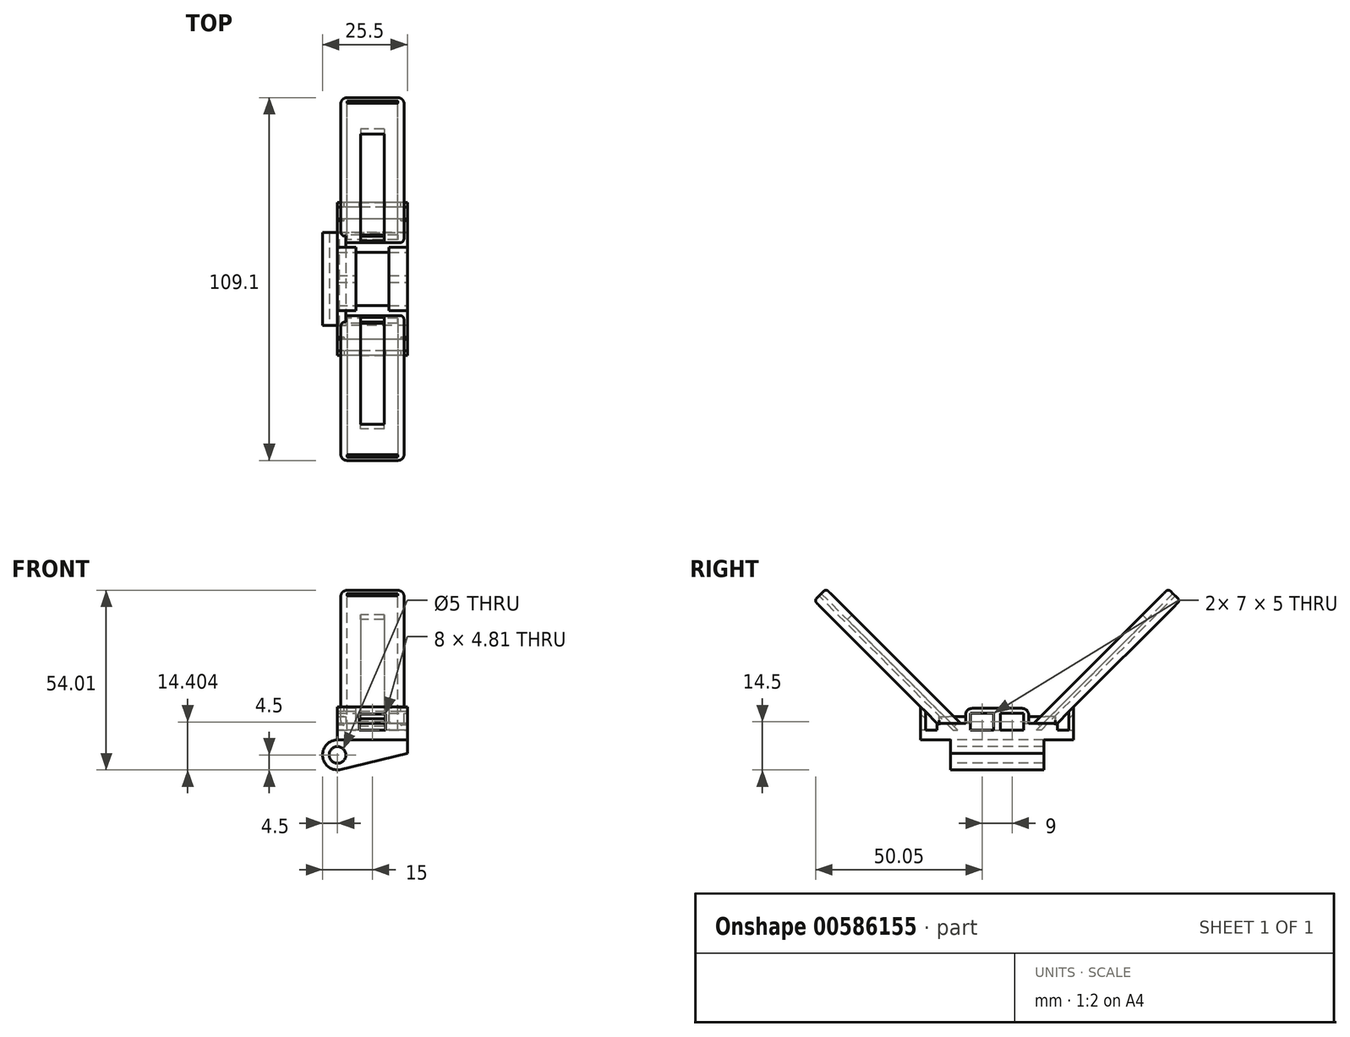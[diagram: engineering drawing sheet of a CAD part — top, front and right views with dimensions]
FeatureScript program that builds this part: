
annotation { "Feature Type Name" : "Feature", "Feature Type Description" : "" }
export const myFeature = defineFeature(function(context is Context, id is Id, definition is map)
    precondition{}
    {
        {
            var Q0;
            Q0=qCreatedBy(makeId("Top.planeOp"),FACE);
            var sketch = newSketch(context, id + "F0", { "sketchPlane" : qUnion([Q0])});
            skLineSegment(sketch, "E0.bottom", {"start": v(-10.5, 23) * mm, "end": v(10.5, 23) * mm});
            skLineSegment(sketch, "E0.top", {"start": v(-10.5, -23) * mm, "end": v(10.5, -23) * mm});
            skLineSegment(sketch, "E0.left", {"start": v(-10.5, 23) * mm, "end": v(-10.5, -23) * mm});
            skLineSegment(sketch, "E0.right", {"start": v(10.5, 23) * mm, "end": v(10.5, -23) * mm});
            skPoint(sketch, "E0.middle", {"position": v(0, 0) * mm});
            skSolve(sketch);
        }
        {
            var Q0;
            Q0=qSketchRegion(id+"F0",true);
            extrude(context, id + "F1", {"entities" : qUnion([Q0]), "oppositeDirection" : true, "depth" : 12 * mm, "offsetDistance" : 25 * mm});
        }
        {
            var Q0;
            Q0=qCreatedBy(makeId("Front.planeOp"),FACE);
            var sketch = newSketch(context, id + "F2", { "sketchPlane" : qUnion([Q0])});
            skCircle(sketch, "E1", {"center": v(-10.5, -7.5) * mm, "radius": 4.5 * mm});
            skPoint(sketch, "E1.first.point", {"position": v(-10.5, -3) * mm});
            skPoint(sketch, "E1.second.point", {"position": v(-10.5, -12) * mm});
            skPoint(sketch, "E1.third.point", {"position": v(-14.85, -8.64) * mm});
            skPoint(sketch, "E2.first.point", {"position": v(10.5, 0) * mm});
            skPoint(sketch, "E2.second.point", {"position": v(10.5, -12) * mm});
            skPoint(sketch, "E2.third.point", {"position": v(4.96, -4.94) * mm});
            skSolve(sketch);
        }
        {
            var Q0;
            Q0=makeQuery(id+"F2.imprint","IMPRINT",FACE,{"disambiguationData":[TD([[makeQuery(id+"F2.imprint","IMPRINT",EDGE,{"derivedFrom":sQuery(id+"F2.wireOp",EDGE,"E1")}),1.0]])]});
            extrude(context, id + "F3", {"entities" : qUnion([Q0]), "operationType" : NewBodyOperationType.ADD, "endBound" : BoundingType.SYMMETRIC, "oppositeDirection" : true, "depth" : 46 * mm, "offsetDistance" : 25 * mm});
        }
        {
            var Q0;
            Q0=qCreatedBy(makeId("Top.planeOp"),FACE);
            var sketch = newSketch(context, id + "F4", { "sketchPlane" : qUnion([Q0])});
            skLineSegment(sketch, "E3", {"start": v(-22.5, -9) * mm, "end": v(32.95, -9) * mm});
            skSolve(sketch);
        }
        {
            var Q0;
            Q0=sQuery(id+"F4.wireOp",EDGE,"E3");
            cPlane(context, id + "F5", {"entities" : qUnion([Q0]), "cplaneType" : CPlaneType.LINE_ANGLE, "offset" : 25 * mm, "angle" : 45 * degree, "width" : 150 * mm, "height" : 150 * mm});
        }
        {
            var Q0;
            Q0=qCreatedBy(id+"F5.planeOp",FACE);
            var sketch = newSketch(context, id + "F6", { "sketchPlane" : qUnion([Q0])});
            skLineSegment(sketch, "E4.bottom", {"start": v(9.5, 6.36) * mm, "end": v(-9.5, 6.36) * mm});
            skLineSegment(sketch, "E4.top", {"start": v(9.5, 66.36) * mm, "end": v(-9.5, 66.36) * mm});
            skLineSegment(sketch, "E4.left", {"start": v(9.5, 6.36) * mm, "end": v(9.5, 66.36) * mm});
            skLineSegment(sketch, "E4.right", {"start": v(-9.5, 6.36) * mm, "end": v(-9.5, 66.36) * mm});
            skSolve(sketch);
        }
        {
            var Q0;
            Q0=qSketchRegion(id+"F6",true);
            extrude(context, id + "F7", {"entities" : qUnion([Q0]), "operationType" : NewBodyOperationType.ADD, "oppositeDirection" : true, "depth" : 5 * mm, "offsetDistance" : 25 * mm});
        }
        {
            var Q0;
            Q0=makeQuery(id+"F7.opExtrude","SWEPT_EDGE",EDGE,{"disambiguationData":[OSD([sQuery(id+"F6.wireOp",EDGE,"E4.top"),sQuery(id+"F6.wireOp",EDGE,"E4.left")])]});
            var Q1;
            Q1=makeQuery(id+"F7.opExtrude","SWEPT_EDGE",EDGE,{"disambiguationData":[OSD([sQuery(id+"F6.wireOp",EDGE,"E4.top"),sQuery(id+"F6.wireOp",EDGE,"E4.right")])]});
            fillet(context, id + "F8", {"entities" : qUnion([Q0, Q1]), "radius" : (2) * mm, "tangentPropagation" : true, "allowEdgeOverflow" : false});
        }
        {
            var Q0;
            Q0=makeQuery(id+"F7.opExtrude","CAP_EDGE",EDGE,{"disambiguationData":[OSD([sQuery(id+"F6.wireOp",EDGE,"E4.right")])],"isStart":true});
            var Q1;
            Q1=makeQuery(id+"F7.opExtrude","CAP_EDGE",EDGE,{"disambiguationData":[OSD([sQuery(id+"F6.wireOp",EDGE,"E4.right")])],"isStart":false});
            var Q2;
            Q2=makeQuery(id+"F7.opExtrude","CAP_EDGE",EDGE,{"disambiguationData":[OSD([sQuery(id+"F6.wireOp",EDGE,"E4.left")])],"isStart":true});
            var Q3;
            Q3=makeQuery(id+"F7.opExtrude","CAP_EDGE",EDGE,{"disambiguationData":[OSD([sQuery(id+"F6.wireOp",EDGE,"E4.left")])],"isStart":false});
            fillet(context, id + "F9", {"entities" : qUnion([Q0, Q1, Q2, Q3]), "radius" : 1 * mm, "tangentPropagation" : true, "allowEdgeOverflow" : false});
        }
        {
            var Q0;
            Q0=qCreatedBy(makeId("Right.planeOp"),FACE);
            var sketch = newSketch(context, id + "F10", { "sketchPlane" : qUnion([Q0])});
            skLineSegment(sketch, "E5.bottom", {"start": v(-9.5, 6.5) * mm, "end": v(9.5, 6.5) * mm});
            skLineSegment(sketch, "E5.top", {"start": v(-9.5, 0) * mm, "end": v(9.5, 0) * mm});
            skLineSegment(sketch, "E5.left", {"start": v(-9.5, 6.5) * mm, "end": v(-9.5, 0) * mm});
            skLineSegment(sketch, "E5.right", {"start": v(9.5, 6.5) * mm, "end": v(9.5, 0) * mm});
            skSolve(sketch);
        }
        {
            var Q0;
            Q0=qSketchRegion(id+"F10",true);
            extrude(context, id + "F11", {"entities" : qUnion([Q0]), "operationType" : NewBodyOperationType.ADD, "endBound" : BoundingType.SYMMETRIC, "depth" : 21 * mm, "offsetDistance" : 25 * mm});
        }
        {
            var Q0;
            Q0=makeQuery(id+"F11.opExtrude","SWEPT_EDGE",EDGE,{"disambiguationData":[OSD([sQuery(id+"F10.wireOp",EDGE,"E5.bottom"),sQuery(id+"F10.wireOp",EDGE,"E5.left")])]});
            var Q1;
            Q1=makeQuery(id+"F11.opExtrude","SWEPT_EDGE",EDGE,{"disambiguationData":[OSD([sQuery(id+"F10.wireOp",EDGE,"E5.bottom"),sQuery(id+"F10.wireOp",EDGE,"E5.right")])]});
            fillet(context, id + "F12", {"entities" : qUnion([Q0, Q1]), "radius" : 2 * mm, "tangentPropagation" : true, "allowEdgeOverflow" : false});
        }
        {
            var Q0;
            Q0=qCreatedBy(makeId("Right.planeOp"),FACE);
            var sketch = newSketch(context, id + "F13", { "sketchPlane" : qUnion([Q0])});
            skLineSegment(sketch, "E6.bottom", {"start": v(-8, 0) * mm, "end": v(-1, 0) * mm});
            skLineSegment(sketch, "E6.top", {"start": v(-8, 5) * mm, "end": v(-1, 5) * mm});
            skLineSegment(sketch, "E6.left", {"start": v(-8, 0) * mm, "end": v(-8, 5) * mm});
            skLineSegment(sketch, "E6.right", {"start": v(-1, 0) * mm, "end": v(-1, 5) * mm});
            skLineSegment(sketch, "E7.bottom", {"start": v(8, 0) * mm, "end": v(1, 0) * mm});
            skLineSegment(sketch, "E7.top", {"start": v(8, 5) * mm, "end": v(1, 5) * mm});
            skLineSegment(sketch, "E7.left", {"start": v(8, 0) * mm, "end": v(8, 5) * mm});
            skLineSegment(sketch, "E7.right", {"start": v(1, 0) * mm, "end": v(1, 5) * mm});
            skSolve(sketch);
        }
        {
            var Q0;
            Q0=qSketchRegion(id+"F13",true);
            extrude(context, id + "F14", {"entities" : qUnion([Q0]), "operationType" : NewBodyOperationType.REMOVE, "endBound" : BoundingType.SYMMETRIC, "oppositeDirection" : true, "depth" : 55 * mm, "offsetDistance" : 25 * mm});
        }
        {
            var Q0;
            Q0=qCreatedBy(makeId("Right.planeOp"),FACE);
            var sketch = newSketch(context, id + "F15", { "sketchPlane" : qUnion([Q0])});
            skLineSegment(sketch, "E8.bottom", {"start": v(-9.5, 0) * mm, "end": v(9.5, 0) * mm});
            skLineSegment(sketch, "E8.top", {"start": v(-9.5, 6.5) * mm, "end": v(9.5, 6.5) * mm});
            skLineSegment(sketch, "E8.left", {"start": v(-9.5, 0) * mm, "end": v(-9.5, 6.5) * mm});
            skLineSegment(sketch, "E8.right", {"start": v(9.5, 0) * mm, "end": v(9.5, 6.5) * mm});
            skSolve(sketch);
        }
        {
            var Q0;
            Q0=qSketchRegion(id+"F15",true);
            extrude(context, id + "F16", {"entities" : qUnion([Q0]), "operationType" : NewBodyOperationType.REMOVE, "endBound" : BoundingType.SYMMETRIC, "oppositeDirection" : true, "depth" : 10 * mm, "offsetDistance" : 25 * mm});
        }
        {
            var Q0;
            Q0=makeQuery(id+"F7.opExtrude","SWEPT_FACE",FACE,{"disambiguationData":[OSD([sQuery(id+"F6.wireOp",EDGE,"E4.top")])]});
            var sketch = newSketch(context, id + "F17", { "sketchPlane" : qUnion([Q0])});
            skLineSegment(sketch, "E9.bottom", {"start": v(-7.6, -8.36) * mm, "end": v(7.6, -8.36) * mm});
            skLineSegment(sketch, "E9.top", {"start": v(-7.6, -9.36) * mm, "end": v(7.6, -9.36) * mm});
            skLineSegment(sketch, "E9.left", {"start": v(-7.6, -8.36) * mm, "end": v(-7.6, -9.36) * mm});
            skLineSegment(sketch, "E9.right", {"start": v(7.6, -8.36) * mm, "end": v(7.6, -9.36) * mm});
            skSolve(sketch);
        }
        {
            var Q0;
            Q0=qSketchRegion(id+"F17",true);
            extrude(context, id + "F18", {"entities" : qUnion([Q0]), "operationType" : NewBodyOperationType.REMOVE, "oppositeDirection" : true, "depth" : 58.5 * mm, "offsetDistance" : 25 * mm});
        }
        {
            var Q0;
            Q0=makeQuery(id+"F7.opExtrude","CAP_FACE",FACE,{"disambiguationData":[OSD([sQuery(id+"F6.wireOp",EDGE,"E4.bottom"),sQuery(id+"F6.wireOp",EDGE,"E4.top"),sQuery(id+"F6.wireOp",EDGE,"E4.left"),sQuery(id+"F6.wireOp",EDGE,"E4.right")])],"isStart":true});
            var sketch = newSketch(context, id + "F19", { "sketchPlane" : qUnion([Q0])});
            skLineSegment(sketch, "E10.bottom", {"start": v(-3.5, 55.36) * mm, "end": v(3.5, 55.36) * mm});
            skLineSegment(sketch, "E10.top", {"start": v(-3.5, 9.86) * mm, "end": v(3.5, 9.86) * mm});
            skLineSegment(sketch, "E10.left", {"start": v(-3.5, 55.36) * mm, "end": v(-3.5, 9.86) * mm});
            skLineSegment(sketch, "E10.right", {"start": v(3.5, 55.36) * mm, "end": v(3.5, 9.86) * mm});
            skSolve(sketch);
        }
        {
            var Q0;
            Q0=qSketchRegion(id+"F19",true);
            extrude(context, id + "F20", {"entities" : qUnion([Q0]), "operationType" : NewBodyOperationType.REMOVE, "oppositeDirection" : true, "depth" : 2 * mm, "offsetDistance" : 25 * mm});
        }
        {
            var Q0;
            Q0=qCreatedBy(makeId("Front.planeOp"),FACE);
            var sketch = newSketch(context, id + "F21", { "sketchPlane" : qUnion([Q0])});
            skCircle(sketch, "E11", {"center": v(-10.5, -7.5) * mm, "radius": 2.5 * mm});
            skSolve(sketch);
        }
        {
            var Q0;
            Q0 = qSketchRegion(id + "F21", true);
            extrude(context, id + "F22", {"entities" : qUnion([Q0]), "operationType" : NewBodyOperationType.REMOVE, "endBound" : BoundingType.SYMMETRIC, "oppositeDirection" : true, "depth" : 46 * mm, "offsetDistance" : 25 * mm});
        }
        {
            var Q0;
            Q0=makeQuery(id+"F3.boolean.opBoolean","MERGE",FACE,{"derivedFrom":[makeQuery(id+"F1.opExtrude","SWEPT_FACE",FACE,{"disambiguationData":[OSD([sQuery(id+"F0.wireOp",EDGE,"E0.top")])]}),makeQuery(id+"F3.opExtrude","CAP_FACE",FACE,{"disambiguationData":[OSD([sQuery(id+"F2.wireOp",EDGE,"E1")])],"isStart":true})]});
            var sketch = newSketch(context, id + "F23", { "sketchPlane" : qUnion([Q0])});
            skLineSegment(sketch, "E12.bottom", {"start": v(20, -12) * mm, "end": v(-20, -12) * mm});
            skLineSegment(sketch, "E12.top", {"start": v(20, -3) * mm, "end": v(-20, -3) * mm});
            skLineSegment(sketch, "E12.left", {"start": v(20, -12) * mm, "end": v(20, -3) * mm});
            skLineSegment(sketch, "E12.right", {"start": v(-20, -12) * mm, "end": v(-20, -3) * mm});
            skSolve(sketch);
        }
        {
            var Q0;
            Q0 = qSketchRegion(id + "F23", true);
            extrude(context, id + "F24", {"entities" : qUnion([Q0]), "operationType" : NewBodyOperationType.REMOVE, "oppositeDirection" : true, "depth" : 9 * mm, "offsetDistance" : 25 * mm});
        }
        {
            var Q0;
            Q0=makeQuery(id+"F3.boolean.opBoolean","MERGE",FACE,{"derivedFrom":[makeQuery(id+"F1.opExtrude","SWEPT_FACE",FACE,{"disambiguationData":[OSD([sQuery(id+"F0.wireOp",EDGE,"E0.bottom")])]}),makeQuery(id+"F3.opExtrude","CAP_FACE",FACE,{"disambiguationData":[OSD([sQuery(id+"F2.wireOp",EDGE,"E1")])],"isStart":false})]});
            var sketch = newSketch(context, id + "F25", { "sketchPlane" : qUnion([Q0])});
            skLineSegment(sketch, "E13.bottom", {"start": v(-20, -3) * mm, "end": v(20, -3) * mm});
            skLineSegment(sketch, "E13.top", {"start": v(-20, -12) * mm, "end": v(20, -12) * mm});
            skLineSegment(sketch, "E13.left", {"start": v(-20, -3) * mm, "end": v(-20, -12) * mm});
            skLineSegment(sketch, "E13.right", {"start": v(20, -3) * mm, "end": v(20, -12) * mm});
            skSolve(sketch);
        }
        {
            var Q0;
            Q0 = qSketchRegion(id + "F25", true);
            extrude(context, id + "F26", {"entities" : qUnion([Q0]), "operationType" : NewBodyOperationType.REMOVE, "oppositeDirection" : true, "depth" : 9 * mm, "offsetDistance" : 25 * mm});
        }
        {
            var Q0;
            Q0=qCreatedBy(makeId("Right.planeOp"),FACE);
            var sketch = newSketch(context, id + "F27", { "sketchPlane" : qUnion([Q0])});
            skLineSegment(sketch, "E14", {"start": v(-18.07, 2) * mm, "end": v(-18.07, 0) * mm});
            skLineSegment(sketch, "E15", {"start": v(-18.07, 0) * mm, "end": v(-16.07, 0) * mm});
            skLineSegment(sketch, "E16", {"start": v(-16.07, 0) * mm, "end": v(-18.07, 2) * mm});
            skLineSegment(sketch, "E17", {"start": v(-23, 0) * mm, "end": v(-23, 6.93) * mm});
            skLineSegment(sketch, "E18", {"start": v(-23, 6.93) * mm, "end": v(-21.57, 5.5) * mm});
            skLineSegment(sketch, "E19", {"start": v(-21.57, 5.5) * mm, "end": v(-21.57, 0) * mm});
            skLineSegment(sketch, "E20", {"start": v(-21.57, 0) * mm, "end": v(-23, 0) * mm});
            skSolve(sketch);
        }
        {
            var Q0;
            Q0 = qSketchRegion(id + "F27", true);
            extrude(context, id + "F28", {"entities" : qUnion([Q0]), "operationType" : NewBodyOperationType.ADD, "endBound" : BoundingType.SYMMETRIC, "depth" : 21 * mm, "offsetDistance" : 25 * mm});
        }
        {
            var Q0;
            Q0=qCreatedBy(makeId("Right.planeOp"),FACE);
            var sketch = newSketch(context, id + "F29", { "sketchPlane" : qUnion([Q0])});
            skLineSegment(sketch, "E21", {"start": v(-23, 4.8) * mm, "end": v(-19.07, 0.88) * mm});
            skLineSegment(sketch, "E22", {"start": v(-19.07, 0.88) * mm, "end": v(-19.07, 0) * mm});
            skLineSegment(sketch, "E23", {"start": v(-19.07, 0) * mm, "end": v(-23, 0) * mm});
            skLineSegment(sketch, "E24", {"start": v(-23, 0) * mm, "end": v(-23, 4.8) * mm});
            skSolve(sketch);
        }
        {
            var Q0;
            Q0 = qSketchRegion(id + "F29", true);
            extrude(context, id + "F30", {"entities" : qUnion([Q0]), "operationType" : NewBodyOperationType.REMOVE, "endBound" : BoundingType.SYMMETRIC, "oppositeDirection" : true, "depth" : 8 * mm, "offsetDistance" : 25 * mm});
        }
        {
            var Q0;
            Q0=makeQuery(id+"F1.opExtrude","SWEPT_BODY",BODY,{"disambiguationData":[OSD([sQuery(id+"F0.wireOp",EDGE,"E0.bottom"),sQuery(id+"F0.wireOp",EDGE,"E0.top"),sQuery(id+"F0.wireOp",EDGE,"E0.left"),sQuery(id+"F0.wireOp",EDGE,"E0.right")])]});
            var Q1;
            Q1=qCreatedBy(makeId("Front.planeOp"),FACE);
            mirror(context, id + "F31", {"entities" : qUnion([Q0]), "mirrorPlane" : qUnion([Q1])});
        }
        {
            var Q0;
            Q0=qCreatedBy(makeId("Right.planeOp"),FACE);
            var sketch = newSketch(context, id + "F32", { "sketchPlane" : qUnion([Q0])});
            skLineSegment(sketch, "E25", {"start": v(11, 2) * mm, "end": v(8, 2) * mm});
            skLineSegment(sketch, "E26", {"start": v(8, 2) * mm, "end": v(8, 0) * mm});
            skLineSegment(sketch, "E27", {"start": v(8, 0) * mm, "end": v(11, 0) * mm});
            skLineSegment(sketch, "E28", {"start": v(11, 0) * mm, "end": v(11, 2) * mm});
            skSolve(sketch);
        }
        {
            var Q0;
            Q0 = qSketchRegion(id + "F32", true);
            extrude(context, id + "F33", {"entities" : qUnion([Q0]), "operationType" : NewBodyOperationType.ADD, "endBound" : BoundingType.SYMMETRIC, "depth" : 21 * mm, "offsetDistance" : 25 * mm});
        }
        {
            var Q0;
            {var subQ1=sQuery(id+"F0.wireOp",EDGE,"E0.right");var subQ2=sQuery(id+"F10.wireOp",EDGE,"E5.left");Q0=makeQuery(id+"F16.boolean.opBoolean","SPLIT",FACE,{"disambiguationData":[TD([makeQuery(id+"F1.opExtrude","SWEPT_FACE",FACE,{"disambiguationData":[OSD([subQ1])]})])],"derivedFrom":makeQuery(id+"F11.opExtrude","SWEPT_FACE",FACE,{"disambiguationData":[OSD([subQ2])]})});}
            var sketch = newSketch(context, id + "F34", { "sketchPlane" : qUnion([Q0])});
            skLineSegment(sketch, "E29.bottom", {"start": v(8, 2) * mm, "end": v(10.5, 2) * mm});
            skLineSegment(sketch, "E29.top", {"start": v(8, 0) * mm, "end": v(10.5, 0) * mm});
            skLineSegment(sketch, "E29.left", {"start": v(8, 2) * mm, "end": v(8, 0) * mm});
            skLineSegment(sketch, "E29.right", {"start": v(10.5, 2) * mm, "end": v(10.5, 0) * mm});
            skSolve(sketch);
        }
        {
            var Q0;
            Q0 = qSketchRegion(id + "F34", true);
            extrude(context, id + "F35", {"entities" : qUnion([Q0]), "operationType" : NewBodyOperationType.ADD, "depth" : 8 * mm, "offsetDistance" : 25 * mm});
        }
        {
            var Q0;
            {var subQ1=sQuery(id+"F0.wireOp",EDGE,"E0.left");var subQ2=sQuery(id+"F10.wireOp",EDGE,"E5.left");Q0=makeQuery(id+"F16.boolean.opBoolean","SPLIT",FACE,{"disambiguationData":[TD([makeQuery(id+"F1.opExtrude","SWEPT_FACE",FACE,{"disambiguationData":[OSD([subQ1])]})])],"derivedFrom":makeQuery(id+"F11.opExtrude","SWEPT_FACE",FACE,{"disambiguationData":[OSD([subQ2])]})});}
            var sketch = newSketch(context, id + "F36", { "sketchPlane" : qUnion([Q0])});
            skLineSegment(sketch, "E30.bottom", {"start": v(-10.5, 3.97) * mm, "end": v(-8, 3.97) * mm});
            skLineSegment(sketch, "E30.top", {"start": v(-10.5, 0) * mm, "end": v(-8, 0) * mm});
            skLineSegment(sketch, "E30.left", {"start": v(-10.5, 3.97) * mm, "end": v(-10.5, 0) * mm});
            skLineSegment(sketch, "E30.right", {"start": v(-8, 3.97) * mm, "end": v(-8, 0) * mm});
            skSolve(sketch);
        }
        {
            var Q0;
            Q0 = qSketchRegion(id + "F36", true);
            extrude(context, id + "F37", {"entities" : qUnion([Q0]), "operationType" : NewBodyOperationType.ADD, "depth" : 8 * mm, "offsetDistance" : 25 * mm});
        }
        {
            var Q0;
            Q0=qCreatedBy(makeId("Front.planeOp"),FACE);
            var sketch = newSketch(context, id + "F38", { "sketchPlane" : qUnion([Q0])});
            skLineSegment(sketch, "E31", {"start": v(-9.96, -12) * mm, "end": v(10.5, -7) * mm});
            skLineSegment(sketch, "E32", {"start": v(10.5, -7) * mm, "end": v(10.5, -12) * mm});
            skLineSegment(sketch, "E33", {"start": v(10.5, -12) * mm, "end": v(-9.96, -12) * mm});
            skSolve(sketch);
        }
        {
            var Q0;
            Q0 = qSketchRegion(id + "F38", true);
            extrude(context, id + "F39", {"entities" : qUnion([Q0]), "operationType" : NewBodyOperationType.REMOVE, "endBound" : BoundingType.SYMMETRIC, "depth" : 36 * mm, "offsetDistance" : 25 * mm});
        }
        {
            var Q0;
            Q0=makeQuery(id+"F1.opExtrude","SWEPT_BODY",BODY,{"disambiguationData":[OSD([sQuery(id+"F0.wireOp",EDGE,"E0.bottom"),sQuery(id+"F0.wireOp",EDGE,"E0.top"),sQuery(id+"F0.wireOp",EDGE,"E0.left"),sQuery(id+"F0.wireOp",EDGE,"E0.right")])]});
            var Q1;
            Q1=qCreatedBy(makeId("Front.planeOp"),FACE);
            mirror(context, id + "F40", {"operationType" : NewBodyOperationType.ADD, "entities" : qUnion([Q0]), "mirrorPlane" : qUnion([Q1])});
        }
    });
